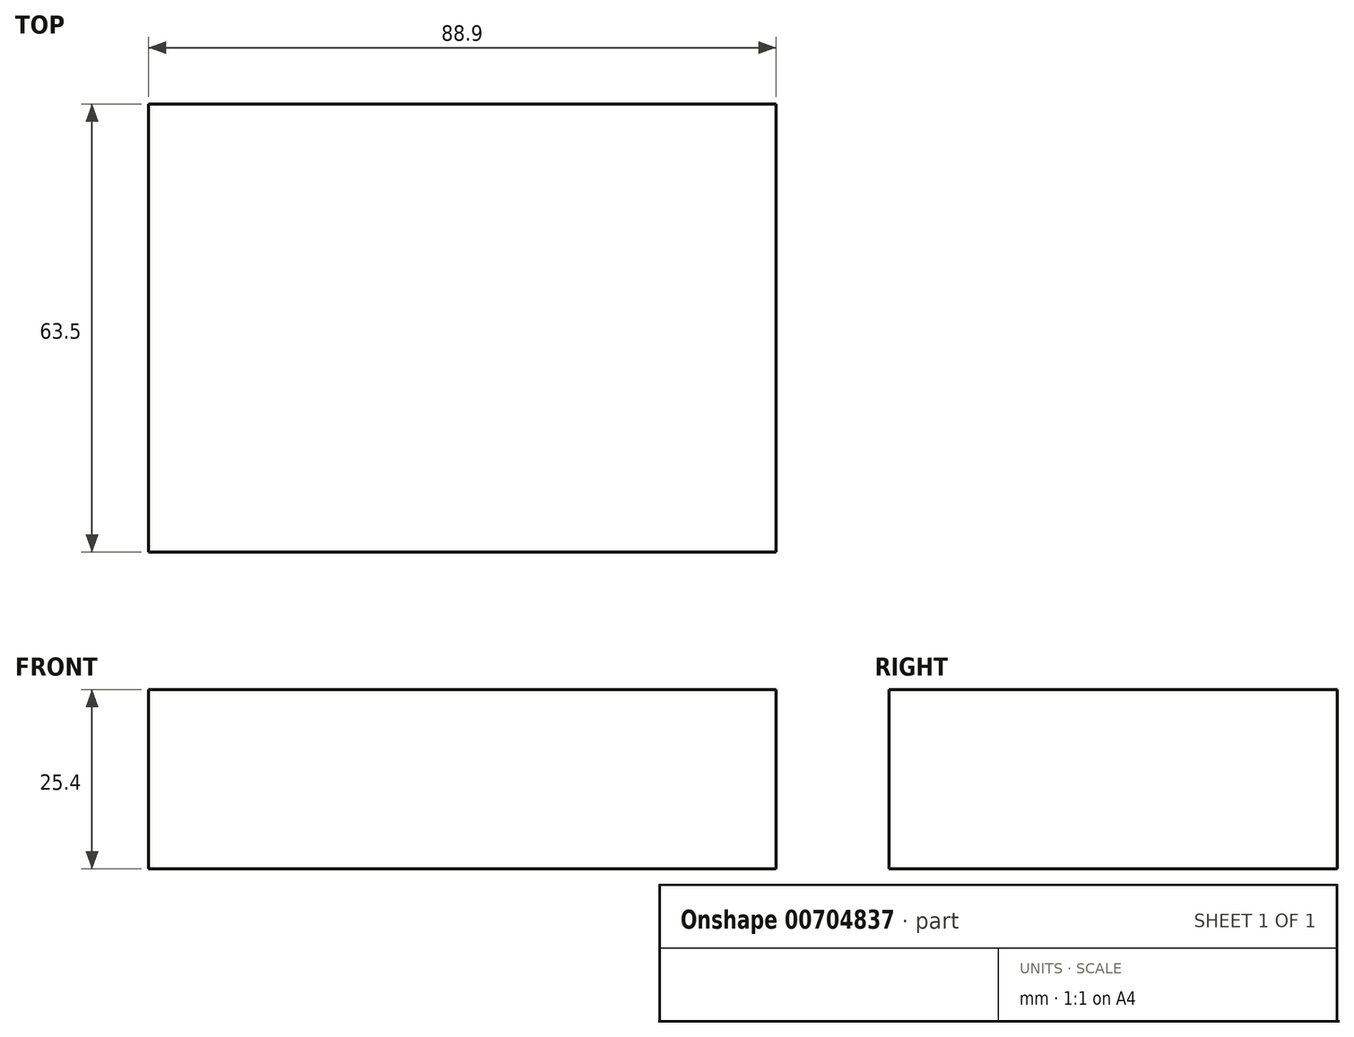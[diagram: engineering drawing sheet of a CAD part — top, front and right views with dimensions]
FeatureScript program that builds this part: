
annotation { "Feature Type Name" : "Feature", "Feature Type Description" : "" }
export const myFeature = defineFeature(function(context is Context, id is Id, definition is map)
    precondition{}
    {
        {
            var Q0;
            Q0=qCreatedBy(makeId("Top.planeOp"),FACE);
            var sketch = newSketch(context, id + "F0", { "sketchPlane" : qUnion([Q0])});
            skLineSegment(sketch, "E0.bottom", {"start": v(-73.84, 41.75) * mm, "end": v(15.06, 41.75) * mm});
            skLineSegment(sketch, "E0.top", {"start": v(-73.84, -21.75) * mm, "end": v(15.06, -21.75) * mm});
            skLineSegment(sketch, "E0.left", {"start": v(-73.84, 41.75) * mm, "end": v(-73.84, -21.75) * mm});
            skLineSegment(sketch, "E0.right", {"start": v(15.06, 41.75) * mm, "end": v(15.06, -21.75) * mm});
            skSolve(sketch);
        }
        {
            var Q0;
            Q0=makeQuery(id+"F0.imprint","IMPRINT",FACE,{"disambiguationData":[TD([[makeQuery(id+"F0.imprint","IMPRINT",EDGE,{"derivedFrom":sQuery(id+"F0.wireOp",EDGE,"E0.bottom")}),-1.0]])]});
            extrude(context, id + "F1", {"entities" : qUnion([Q0]), "depth" : 25.4 * mm, "offsetDistance" : 25.4 * mm});
        }
    });
